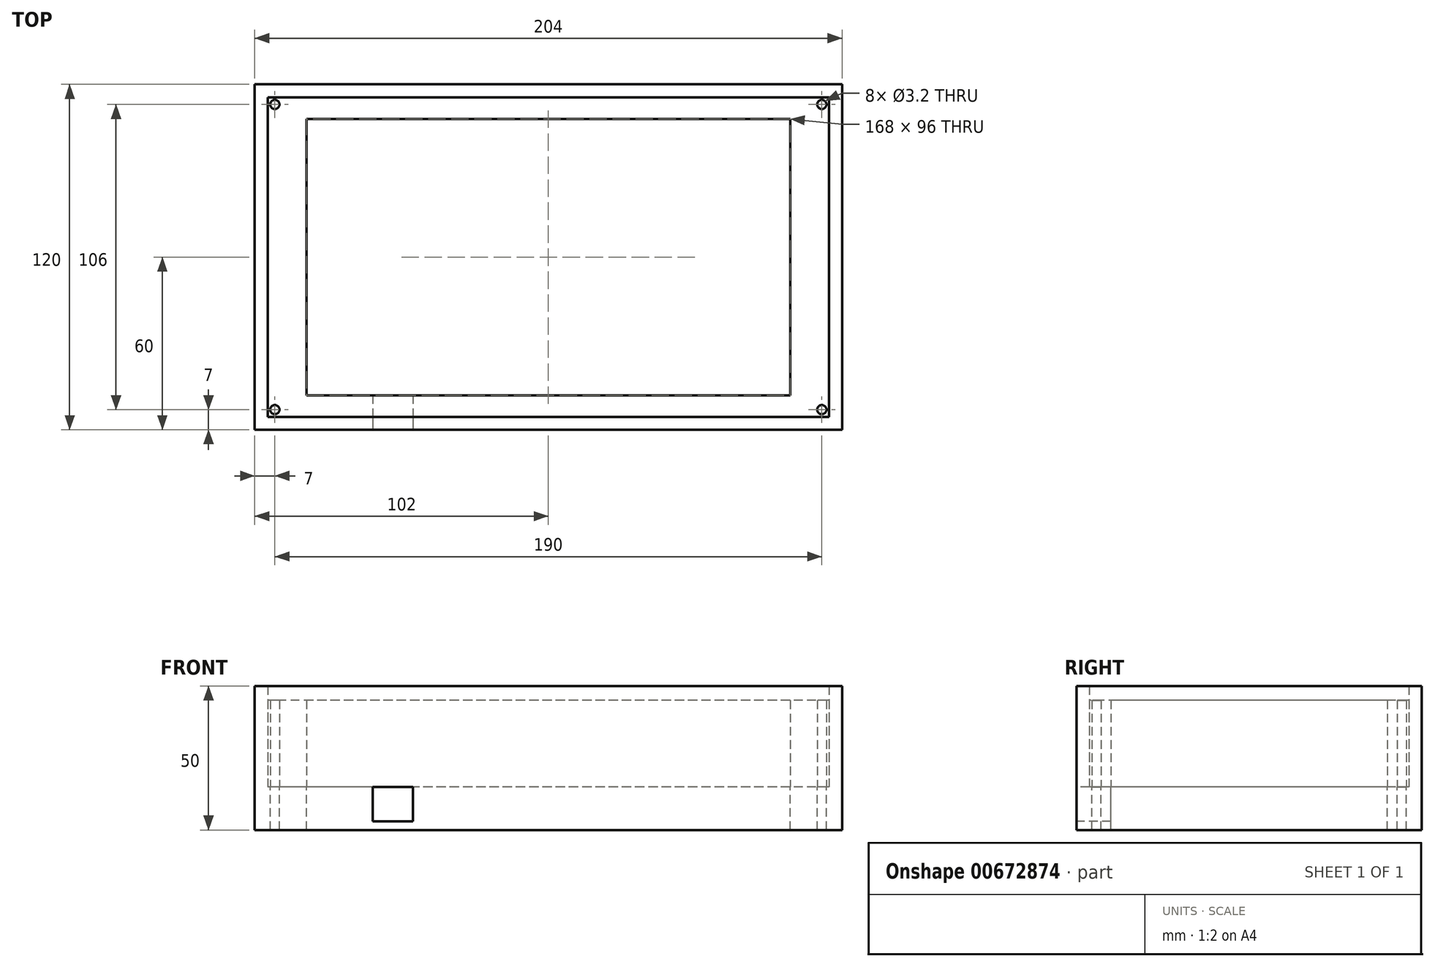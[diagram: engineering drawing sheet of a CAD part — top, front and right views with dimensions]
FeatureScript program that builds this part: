
annotation { "Feature Type Name" : "Feature", "Feature Type Description" : "" }
export const myFeature = defineFeature(function(context is Context, id is Id, definition is map)
    precondition{}
    {
        {
            var Q0;
            Q0=qCreatedBy(makeId("Top.planeOp"),FACE);
            var sketch = newSketch(context, id + "F0", { "sketchPlane" : qUnion([Q0])});
            skLineSegment(sketch, "E0.bottom", {"start": v(102, 60) * mm, "end": v(-102, 60) * mm});
            skLineSegment(sketch, "E0.top", {"start": v(102, -60) * mm, "end": v(-102, -60) * mm});
            skLineSegment(sketch, "E0.left", {"start": v(102, 60) * mm, "end": v(102, -60) * mm});
            skLineSegment(sketch, "E0.right", {"start": v(-102, 60) * mm, "end": v(-102, -60) * mm});
            skPoint(sketch, "E0.middle", {"position": v(0, 0) * mm});
            skLineSegment(sketch, "E1.bottom", {"start": v(84, 48) * mm, "end": v(-84, 48) * mm});
            skLineSegment(sketch, "E1.top", {"start": v(84, -48) * mm, "end": v(-84, -48) * mm});
            skLineSegment(sketch, "E1.left", {"start": v(84, 48) * mm, "end": v(84, -48) * mm});
            skLineSegment(sketch, "E1.right", {"start": v(-84, 48) * mm, "end": v(-84, -48) * mm});
            skLineSegment(sketch, "E2.bottom", {"start": v(97.5, 55.5) * mm, "end": v(-97.5, 55.5) * mm});
            skLineSegment(sketch, "E2.top", {"start": v(97.5, -55.5) * mm, "end": v(-97.5, -55.5) * mm});
            skLineSegment(sketch, "E2.left", {"start": v(97.5, 55.5) * mm, "end": v(97.5, -55.5) * mm});
            skLineSegment(sketch, "E2.right", {"start": v(-97.5, 55.5) * mm, "end": v(-97.5, -55.5) * mm});
            skLineSegment(sketch, "E3.bottom", {"start": v(-102, 60) * mm, "end": v(-95, 60) * mm});
            skLineSegment(sketch, "E3.left", {"start": v(-102, 60) * mm, "end": v(-102, 53) * mm});
            skCircle(sketch, "E4", {"center": v(-95, 53) * mm, "radius": 1.6 * mm});
            skLineSegment(sketch, "E5.bottom", {"start": v(102, 60) * mm, "end": v(95, 60) * mm});
            skLineSegment(sketch, "E5.left", {"start": v(102, 60) * mm, "end": v(102, 53) * mm});
            skCircle(sketch, "E6", {"center": v(95, 53) * mm, "radius": 1.6 * mm});
            skLineSegment(sketch, "E7.bottom", {"start": v(-102, -60) * mm, "end": v(-95, -60) * mm});
            skLineSegment(sketch, "E7.left", {"start": v(-102, -60) * mm, "end": v(-102, -53) * mm});
            skCircle(sketch, "E8", {"center": v(-95, -53) * mm, "radius": 1.6 * mm});
            skLineSegment(sketch, "E9.bottom", {"start": v(102, -60) * mm, "end": v(95, -60) * mm});
            skLineSegment(sketch, "E9.left", {"start": v(102, -60) * mm, "end": v(102, -53) * mm});
            skCircle(sketch, "E10", {"center": v(95, -53) * mm, "radius": 1.6 * mm});
            skSolve(sketch);
        }
        {
            var Q0;
            Q0=makeQuery(id+"F0.imprint","IMPRINT",FACE,{"disambiguationData":[TD([[makeQuery(id+"F0.imprint","IMPRINT",EDGE,{"derivedFrom":sQuery(id+"F0.wireOp",EDGE,"E0.bottom")}),1.0]])]});
            extrude(context, id + "F1", {"entities" : qUnion([Q0]), "depth" : -15 * mm, "offsetDistance" : 25 * mm});
        }
        {
            var Q0;
            Q0=makeQuery(id+"F0.imprint","IMPRINT",FACE,{"disambiguationData":[TD([[makeQuery(id+"F0.imprint","IMPRINT",EDGE,{"derivedFrom":sQuery(id+"F0.wireOp",EDGE,"E1.bottom")}),-1.0]])]});
            extrude(context, id + "F2", {"entities" : qUnion([Q0]), "operationType" : NewBodyOperationType.ADD, "depth" : -15 * mm, "offsetDistance" : 25 * mm});
        }
        {
            var Q0;
            Q0=makeQuery(id+"F0.imprint","IMPRINT",FACE,{"disambiguationData":[TD([[makeQuery(id+"F0.imprint","IMPRINT",EDGE,{"derivedFrom":sQuery(id+"F0.wireOp",EDGE,"E0.bottom")}),1.0]])]});
            extrude(context, id + "F3", {"entities" : qUnion([Q0]), "operationType" : NewBodyOperationType.ADD, "depth" : 35 * mm, "offsetDistance" : 25 * mm});
        }
        {
            var Q0;
            Q0=makeQuery(id+"F0.imprint","IMPRINT",FACE,{"disambiguationData":[TD([[makeQuery(id+"F0.imprint","IMPRINT",EDGE,{"derivedFrom":sQuery(id+"F0.wireOp",EDGE,"E6")}),1.0]])]});
            extrude(context, id + "F4", {"entities" : qUnion([Q0]), "depth" : 30 * mm, "offsetDistance" : 25 * mm});
        }
        {
            var Q0;
            Q0=makeQuery(id+"F0.imprint","IMPRINT",FACE,{"disambiguationData":[TD([[makeQuery(id+"F0.imprint","IMPRINT",EDGE,{"derivedFrom":sQuery(id+"F0.wireOp",EDGE,"E4")}),1.0]])]});
            extrude(context, id + "F5", {"entities" : qUnion([Q0]), "depth" : 30 * mm, "offsetDistance" : 25 * mm});
        }
        {
            var Q0;
            Q0=makeQuery(id+"F0.imprint","IMPRINT",FACE,{"disambiguationData":[TD([[makeQuery(id+"F0.imprint","IMPRINT",EDGE,{"derivedFrom":sQuery(id+"F0.wireOp",EDGE,"E10")}),1.0]])]});
            extrude(context, id + "F6", {"entities" : qUnion([Q0]), "depth" : 30 * mm, "offsetDistance" : 25 * mm});
        }
        {
            var Q0;
            Q0=makeQuery(id+"F0.imprint","IMPRINT",FACE,{"disambiguationData":[TD([[makeQuery(id+"F0.imprint","IMPRINT",EDGE,{"derivedFrom":sQuery(id+"F0.wireOp",EDGE,"E8")}),1.0]])]});
            extrude(context, id + "F7", {"entities" : qUnion([Q0]), "depth" : 30 * mm, "offsetDistance" : 25 * mm});
        }
        {
            var Q0;
            Q0=makeQuery(id+"F0.imprint","IMPRINT",FACE,{"disambiguationData":[TD([[makeQuery(id+"F0.imprint","IMPRINT",EDGE,{"derivedFrom":sQuery(id+"F0.wireOp",EDGE,"E1.bottom")}),-1.0]])]});
            extrude(context, id + "F8", {"entities" : qUnion([Q0]), "depth" : 30 * mm, "offsetDistance" : 25 * mm});
        }
        {
            var Q0;
            {var subQ0=sQuery(id+"F0.wireOp",EDGE,"E9.bottom");var subQ1=sQuery(id+"F0.wireOp",EDGE,"E7.bottom");var subQ2=sQuery(id+"F0.wireOp",EDGE,"E0.top");Q0=makeQuery(id+"F3.boolean.opBoolean","MERGE",FACE,{"derivedFrom":[makeQuery(id+"F1.opExtrude","SWEPT_FACE",FACE,{"disambiguationData":[OSD([subQ2,subQ1,subQ0])]}),makeQuery(id+"F3.opExtrude","SWEPT_FACE",FACE,{"disambiguationData":[OSD([subQ2,subQ1,subQ0])]})]});}
            var sketch = newSketch(context, id + "F9", { "sketchPlane" : qUnion([Q0])});
            skLineSegment(sketch, "E11.bottom", {"start": v(-102, -15) * mm, "end": v(-54, -15) * mm});
            skLineSegment(sketch, "E11.left", {"start": v(-102, -15) * mm, "end": v(-102, -6) * mm});
            skLineSegment(sketch, "E12.bottom", {"start": v(-47, 0) * mm, "end": v(-61, 0) * mm});
            skLineSegment(sketch, "E12.top", {"start": v(-47, -12) * mm, "end": v(-61, -12) * mm});
            skLineSegment(sketch, "E12.left", {"start": v(-47, 0) * mm, "end": v(-47, -12) * mm});
            skLineSegment(sketch, "E12.right", {"start": v(-61, 0) * mm, "end": v(-61, -12) * mm});
            skPoint(sketch, "E12.middle", {"position": v(-54, -6) * mm});
            skSolve(sketch);
        }
        {
            var Q0;
            Q0=makeQuery(id+"F9.imprint","IMPRINT",FACE,{"disambiguationData":[TD([[makeQuery(id+"F9.imprint","IMPRINT",EDGE,{"derivedFrom":sQuery(id+"F9.wireOp",EDGE,"E12.bottom")}),1.0]])]});
            extrude(context, id + "F10", {"entities" : qUnion([Q0]), "operationType" : NewBodyOperationType.REMOVE, "oppositeDirection" : true, "depth" : 25 * mm, "offsetDistance" : 25 * mm});
        }
    });
